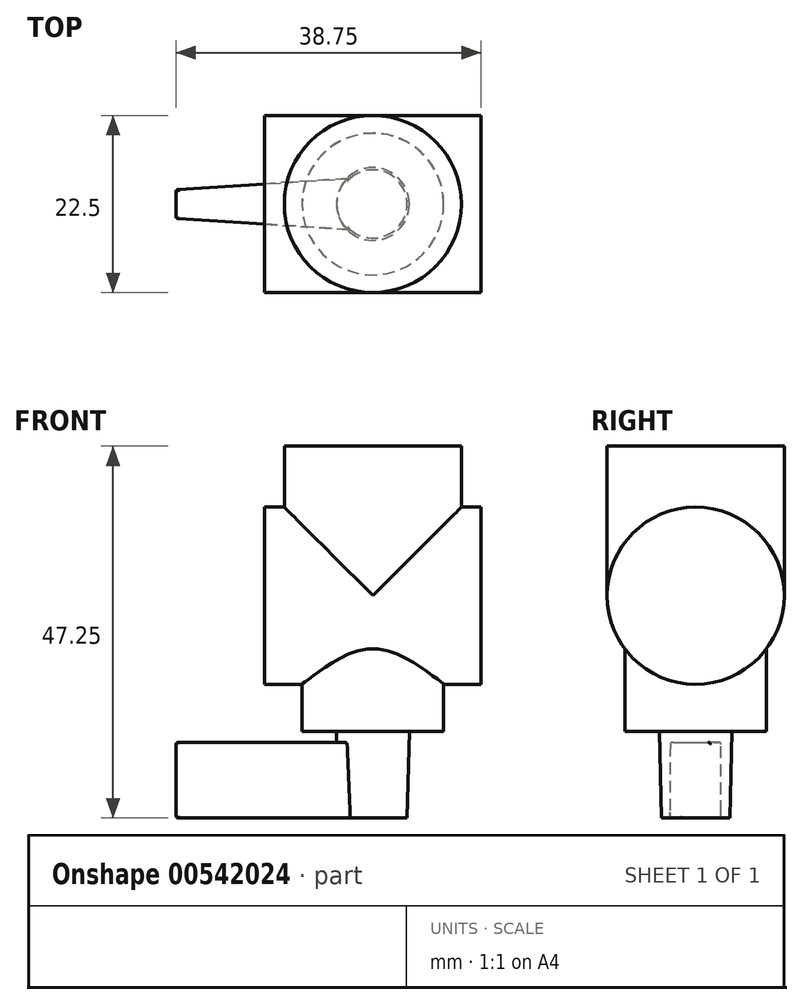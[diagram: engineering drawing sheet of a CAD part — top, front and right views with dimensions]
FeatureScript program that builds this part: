
annotation { "Feature Type Name" : "Feature", "Feature Type Description" : "" }
export const myFeature = defineFeature(function(context is Context, id is Id, definition is map)
    precondition{}
    {
        {
            var Q0;
            Q0=qCreatedBy(makeId("Top.planeOp"),FACE);
            var sketch = newSketch(context, id + "F0", { "sketchPlane" : qUnion([Q0])});
            skCircle(sketch, "E0", {"center": v(0, 0) * mm, "radius": 11.25 * mm});
            skSolve(sketch);
        }
        {
            var Q0;
            Q0=qSketchRegion(id+"F0",true);
            extrude(context, id + "F1", {"entities" : qUnion([Q0]), "oppositeDirection" : true, "depth" : 19 * mm});
        }
        {
            var Q0;
            Q0=qCreatedBy(makeId("Right.planeOp"),FACE);
            var sketch = newSketch(context, id + "F2", { "sketchPlane" : qUnion([Q0])});
            skCircle(sketch, "E1", {"center": v(0, -19) * mm, "radius": 11.25 * mm});
            skSolve(sketch);
        }
        {
            var Q0;
            Q0=qSketchRegion(id+"F2",true);
            extrude(context, id + "F3", {"entities" : qUnion([Q0]), "operationType" : NewBodyOperationType.ADD, "endBound" : BoundingType.SYMMETRIC, "depth" : 27.5 * mm});
        }
        {
            var Q0;
            Q0=qCreatedBy(makeId("Top.planeOp"),FACE);
            var sketch = newSketch(context, id + "F4", { "sketchPlane" : qUnion([Q0])});
            skCircle(sketch, "E2", {"center": v(0, 0) * mm, "radius": 9 * mm});
            skSolve(sketch);
        }
        {
            var Q0;
            Q0=qSketchRegion(id+"F4",true);
            extrude(context, id + "F5", {"entities" : qUnion([Q0]), "operationType" : NewBodyOperationType.ADD, "oppositeDirection" : true, "depth" : 36.25 * mm});
        }
        {
            var Q0;
            Q0=makeQuery(id+"F5.opExtrude","CAP_FACE",FACE,{"disambiguationData":[OSD([sQuery(id+"F4.wireOp",EDGE,"E2")])],"isStart":false});
            var sketch = newSketch(context, id + "F6", { "sketchPlane" : qUnion([Q0])});
            skCircle(sketch, "E3", {"center": v(0, 0) * mm, "radius": 4.62 * mm});
            skSolve(sketch);
        }
        {
            var Q0;
            Q0=qSketchRegion(id+"F6",true);
            extrude(context, id + "F7", {"entities" : qUnion([Q0]), "operationType" : NewBodyOperationType.ADD, "depth" : 11 * mm, "hasDraft" : true, "draftAngle" : 1.5 * degree, "draftPullDirection" : true});
        }
        {
            var Q0;
            Q0=qCreatedBy(makeId("Right.planeOp"),FACE);
            var sketch = newSketch(context, id + "F8", { "sketchPlane" : qUnion([Q0])});
            skLineSegment(sketch, "E4", {"start": v(0, -47.28) * mm, "end": v(0, -37.58) * mm, "construction": true});
            skLineSegment(sketch, "E5.bottom", {"start": v(-3.25, -47.25) * mm, "end": v(3.25, -47.25) * mm});
            skLineSegment(sketch, "E5.top", {"start": v(-3.25, -37.61) * mm, "end": v(3.25, -37.61) * mm});
            skLineSegment(sketch, "E5.left", {"start": v(-3.25, -47.25) * mm, "end": v(-3.25, -37.61) * mm});
            skLineSegment(sketch, "E5.right", {"start": v(3.25, -47.25) * mm, "end": v(3.25, -37.61) * mm});
            skPoint(sketch, "E5.middle", {"position": v(0, -42.43) * mm});
            skSolve(sketch);
        }
        {
            var Q0;
            Q0=qSketchRegion(id+"F8",true);
            extrude(context, id + "F9", {"entities" : qUnion([Q0]), "operationType" : NewBodyOperationType.ADD, "oppositeDirection" : true, "depth" : 25 * mm});
        }
        {
            var Q0;
            Q0=makeQuery(id+"F9.opExtrude","CAP_EDGE",EDGE,{"disambiguationData":[OSD([sQuery(id+"F8.wireOp",EDGE,"E5.right")])],"isStart":false});
            var Q1;
            Q1=makeQuery(id+"F9.opExtrude","CAP_EDGE",EDGE,{"disambiguationData":[OSD([sQuery(id+"F8.wireOp",EDGE,"E5.left")])],"isStart":false});
            chamfer(context, id + "F10", {"entities" : qUnion([Q0, Q1]), "chamferType" : ChamferType.TWO_OFFSETS, "width1" : 22.1 * mm, "oppositeDirection" : false, "width2" : 1.4 * mm, "tangentPropagation" : true});
        }
        {
            var Q0;
            {var subQ0=sQuery(id+"F8.wireOp",EDGE,"E5.right");Q0=makeQuery(id+"F10.opChamfer","BLEND_EDGE",EDGE,{"blendedFrom":[makeQuery(id+"F9.opExtrude","CAP_EDGE",EDGE,{"disambiguationData":[OSD([subQ0])],"isStart":false}),makeQuery(id+"F9.opExtrude","CAP_FACE",FACE,{"disambiguationData":[OSD([sQuery(id+"F8.wireOp",EDGE,"E5.bottom"),sQuery(id+"F8.wireOp",EDGE,"E5.top"),sQuery(id+"F8.wireOp",EDGE,"E5.left"),subQ0])],"isStart":false})],"blendedInto":[makeQuery(id+"F9.opExtrude","CAP_FACE",FACE,{"disambiguationData":[OSD([sQuery(id+"F8.wireOp",EDGE,"E5.bottom"),sQuery(id+"F8.wireOp",EDGE,"E5.top"),sQuery(id+"F8.wireOp",EDGE,"E5.left"),subQ0])],"isStart":false})]});}
            var Q1;
            {var subQ0=sQuery(id+"F8.wireOp",EDGE,"E5.left");Q1=makeQuery(id+"F10.opChamfer","BLEND_EDGE",EDGE,{"blendedFrom":[makeQuery(id+"F9.opExtrude","CAP_EDGE",EDGE,{"disambiguationData":[OSD([subQ0])],"isStart":false}),makeQuery(id+"F9.opExtrude","CAP_FACE",FACE,{"disambiguationData":[OSD([sQuery(id+"F8.wireOp",EDGE,"E5.bottom"),sQuery(id+"F8.wireOp",EDGE,"E5.top"),subQ0,sQuery(id+"F8.wireOp",EDGE,"E5.right")])],"isStart":false})],"blendedInto":[makeQuery(id+"F9.opExtrude","CAP_FACE",FACE,{"disambiguationData":[OSD([sQuery(id+"F8.wireOp",EDGE,"E5.bottom"),sQuery(id+"F8.wireOp",EDGE,"E5.top"),subQ0,sQuery(id+"F8.wireOp",EDGE,"E5.right")])],"isStart":false})]});}
            var Q2;
            Q2=makeQuery(id+"F9.opExtrude","CAP_EDGE",EDGE,{"disambiguationData":[OSD([sQuery(id+"F8.wireOp",EDGE,"E5.bottom")])],"isStart":false});
            var Q3;
            Q3=makeQuery(id+"F10.opChamfer","BLEND_EDGE",EDGE,{"blendedFrom":[makeQuery(id+"F9.opExtrude","CAP_EDGE",EDGE,{"disambiguationData":[OSD([sQuery(id+"F8.wireOp",EDGE,"E5.right")])],"isStart":false}),makeQuery(id+"F9.opExtrude","SWEPT_FACE",FACE,{"disambiguationData":[OSD([sQuery(id+"F8.wireOp",EDGE,"E5.bottom")])]})],"blendedInto":[makeQuery(id+"F9.opExtrude","SWEPT_FACE",FACE,{"disambiguationData":[OSD([sQuery(id+"F8.wireOp",EDGE,"E5.bottom")])]})]});
            var Q4;
            Q4=makeQuery(id+"F10.opChamfer","BLEND_EDGE",EDGE,{"blendedFrom":[makeQuery(id+"F9.opExtrude","CAP_EDGE",EDGE,{"disambiguationData":[OSD([sQuery(id+"F8.wireOp",EDGE,"E5.left")])],"isStart":false}),makeQuery(id+"F9.opExtrude","SWEPT_FACE",FACE,{"disambiguationData":[OSD([sQuery(id+"F8.wireOp",EDGE,"E5.bottom")])]})],"blendedInto":[makeQuery(id+"F9.opExtrude","SWEPT_FACE",FACE,{"disambiguationData":[OSD([sQuery(id+"F8.wireOp",EDGE,"E5.bottom")])]})]});
            var Q5;
            Q5=makeQuery(id+"F10.opChamfer","BLEND_EDGE",EDGE,{"blendedFrom":[makeQuery(id+"F9.opExtrude","CAP_EDGE",EDGE,{"disambiguationData":[OSD([sQuery(id+"F8.wireOp",EDGE,"E5.right")])],"isStart":false}),makeQuery(id+"F9.opExtrude","SWEPT_FACE",FACE,{"disambiguationData":[OSD([sQuery(id+"F8.wireOp",EDGE,"E5.top")])]})],"blendedInto":[makeQuery(id+"F9.opExtrude","SWEPT_FACE",FACE,{"disambiguationData":[OSD([sQuery(id+"F8.wireOp",EDGE,"E5.top")])]})]});
            var Q6;
            Q6=makeQuery(id+"F9.opExtrude","CAP_EDGE",EDGE,{"disambiguationData":[OSD([sQuery(id+"F8.wireOp",EDGE,"E5.top")])],"isStart":false});
            var Q7;
            Q7=makeQuery(id+"F10.opChamfer","BLEND_EDGE",EDGE,{"blendedFrom":[makeQuery(id+"F9.opExtrude","CAP_EDGE",EDGE,{"disambiguationData":[OSD([sQuery(id+"F8.wireOp",EDGE,"E5.left")])],"isStart":false}),makeQuery(id+"F9.opExtrude","SWEPT_FACE",FACE,{"disambiguationData":[OSD([sQuery(id+"F8.wireOp",EDGE,"E5.top")])]})],"blendedInto":[makeQuery(id+"F9.opExtrude","SWEPT_FACE",FACE,{"disambiguationData":[OSD([sQuery(id+"F8.wireOp",EDGE,"E5.top")])]})]});
            fillet(context, id + "F11", {"entities" : qUnion([Q0, Q1, Q2, Q3, Q4, Q5, Q6, Q7]), "radius" : .3 * mm, "tangentPropagation" : true, "allowEdgeOverflow" : false});
        }
    });
